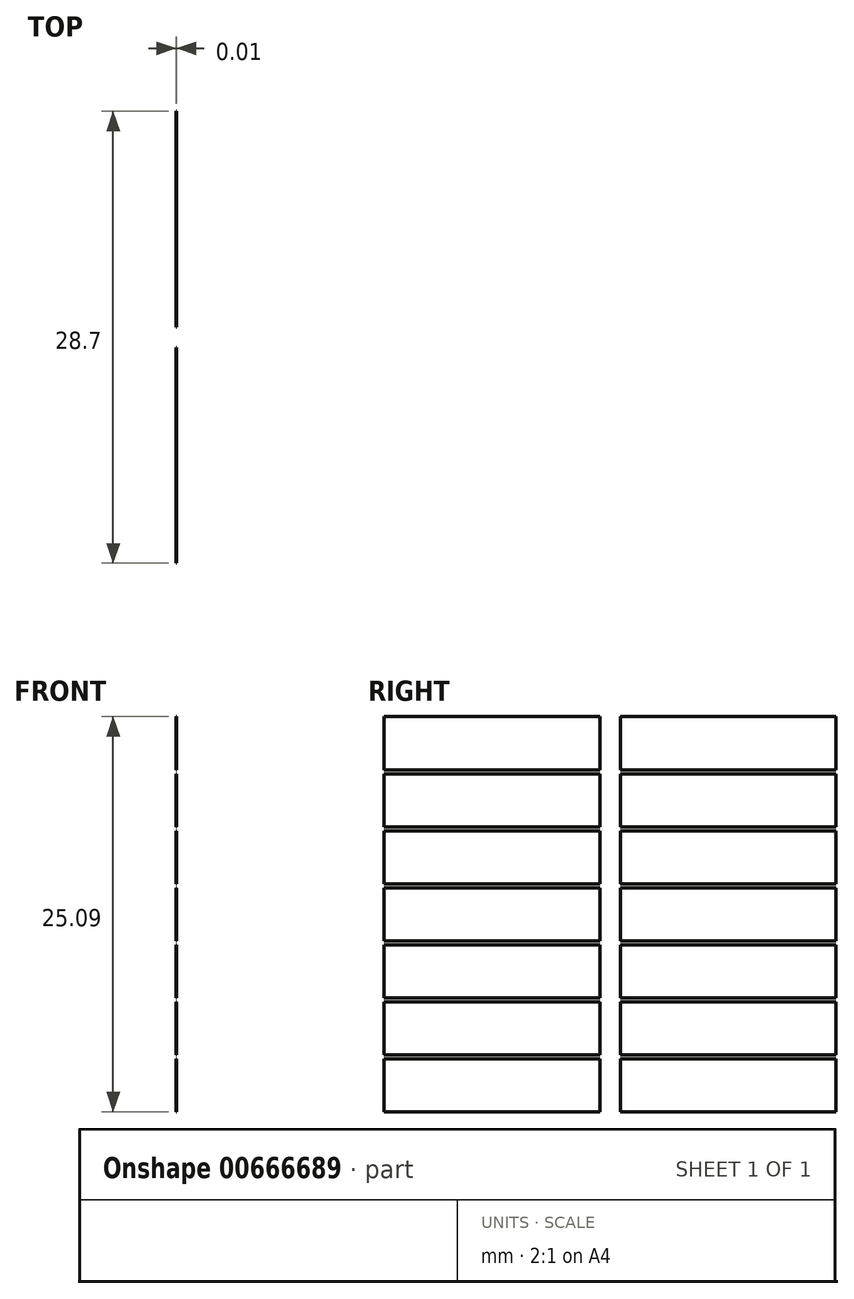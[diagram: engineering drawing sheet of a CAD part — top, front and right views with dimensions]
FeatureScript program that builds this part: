
annotation { "Feature Type Name" : "Feature", "Feature Type Description" : "" }
export const myFeature = defineFeature(function(context is Context, id is Id, definition is map)
    precondition{}
    {
        {
            var Q0;
            Q0=qCreatedBy(makeId("Right.planeOp"),FACE);
            var sketch = newSketch(context, id + "F0", { "sketchPlane" : qUnion([Q0])});
            skPoint(sketch, "E0.0", {"position": v(0, 0) * mm});
            skLineSegment(sketch, "E1.bottom", {"start": v(0, 0) * mm, "end": v(30, 0) * mm});
            skLineSegment(sketch, "E1.top", {"start": v(0, -30) * mm, "end": v(30, -30) * mm});
            skLineSegment(sketch, "E1.left", {"start": v(0, 0) * mm, "end": v(0, -30) * mm});
            skLineSegment(sketch, "E1.right", {"start": v(30, 0) * mm, "end": v(30, -30) * mm});
            skLineSegment(sketch, "E2.1", {"start": v(0.65, -0.65) * mm, "end": v(14.35, -0.65) * mm});
            skLineSegment(sketch, "E2.2", {"start": v(0.65, -0.65) * mm, "end": v(0.65, -2.2) * mm});
            skLineSegment(sketch, "E3", {"start": v(14.35, -2.2) * mm, "end": v(14.35, -0.65) * mm});
            skPoint(sketch, "E4.MirrorP", {"position": v(11.5, 0) * mm});
            skPoint(sketch, "E5.orphan", {"position": v(11.5, -26.74) * mm});
            skPoint(sketch, "E6.orphan", {"position": v(0, -26.74) * mm});
            skLineSegment(sketch, "E7", {"start": v(0.65, -2.46) * mm, "end": v(0.65, -4.02) * mm});
            skLineSegment(sketch, "E8", {"start": v(0.65, -4.02) * mm, "end": v(14.35, -4.02) * mm});
            skLineSegment(sketch, "E9", {"start": v(14.35, -4.02) * mm, "end": v(14.35, -2.46) * mm});
            skLineSegment(sketch, "E10.0", {"start": v(0.65, -4.27) * mm, "end": v(14.35, -4.27) * mm});
            skLineSegment(sketch, "E11", {"start": v(0.65, -4.27) * mm, "end": v(0.65, -5.83) * mm});
            skLineSegment(sketch, "E12", {"start": v(14.35, -5.83) * mm, "end": v(14.35, -4.27) * mm});
            skLineSegment(sketch, "E13.0", {"start": v(0.65, -7.64) * mm, "end": v(14.35, -7.64) * mm});
            skLineSegment(sketch, "E14", {"start": v(0.65, -6.08) * mm, "end": v(0.65, -7.64) * mm});
            skLineSegment(sketch, "E15", {"start": v(14.35, -6.08) * mm, "end": v(14.35, -7.64) * mm});
            skLineSegment(sketch, "E16.0", {"start": v(0.65, -7.9) * mm, "end": v(14.35, -7.9) * mm});
            skLineSegment(sketch, "E17", {"start": v(0.65, -7.9) * mm, "end": v(0.65, -9.45) * mm});
            skLineSegment(sketch, "E18", {"start": v(14.35, -9.45) * mm, "end": v(14.35, -7.9) * mm});
            skLineSegment(sketch, "E19.0", {"start": v(0.65, -11.26) * mm, "end": v(14.35, -11.26) * mm});
            skLineSegment(sketch, "E20", {"start": v(0.65, -9.7) * mm, "end": v(0.65, -11.26) * mm});
            skLineSegment(sketch, "E21", {"start": v(14.35, -9.7) * mm, "end": v(14.35, -11.26) * mm});
            skLineSegment(sketch, "E22.0", {"start": v(0.65, -11.51) * mm, "end": v(14.35, -11.51) * mm});
            skLineSegment(sketch, "E23", {"start": v(0.65, -11.51) * mm, "end": v(0.65, -13.07) * mm});
            skLineSegment(sketch, "E24", {"start": v(14.35, -13.07) * mm, "end": v(14.35, -11.51) * mm});
            skLineSegment(sketch, "E25.0", {"start": v(0.65, -14.88) * mm, "end": v(14.35, -14.88) * mm});
            skLineSegment(sketch, "E26", {"start": v(0.65, -13.32) * mm, "end": v(0.65, -14.88) * mm});
            skLineSegment(sketch, "E27", {"start": v(14.35, -14.88) * mm, "end": v(14.35, -13.32) * mm});
            skLineSegment(sketch, "E28.0", {"start": v(0.65, -15.13) * mm, "end": v(14.35, -15.13) * mm});
            skLineSegment(sketch, "E29", {"start": v(0.65, -15.13) * mm, "end": v(0.65, -16.7) * mm});
            skLineSegment(sketch, "E30", {"start": v(14.35, -16.7) * mm, "end": v(14.35, -15.13) * mm});
            skLineSegment(sketch, "E31.0", {"start": v(0.65, -18.5) * mm, "end": v(14.35, -18.5) * mm});
            skLineSegment(sketch, "E32", {"start": v(0.65, -16.7) * mm, "end": v(0.65, -18.5) * mm});
            skLineSegment(sketch, "E33", {"start": v(14.35, -18.5) * mm, "end": v(14.35, -16.94) * mm});
            skLineSegment(sketch, "E34.0", {"start": v(0.65, -18.75) * mm, "end": v(14.35, -18.75) * mm});
            skLineSegment(sketch, "E35", {"start": v(0.65, -18.75) * mm, "end": v(0.65, -20.31) * mm});
            skLineSegment(sketch, "E36", {"start": v(14.35, -18.75) * mm, "end": v(14.35, -20.31) * mm});
            skLineSegment(sketch, "E37.0", {"start": v(0.65, -22.12) * mm, "end": v(14.35, -22.12) * mm});
            skLineSegment(sketch, "E38", {"start": v(0.65, -20.56) * mm, "end": v(0.65, -22.12) * mm});
            skLineSegment(sketch, "E39", {"start": v(14.35, -20.56) * mm, "end": v(14.35, -22.12) * mm});
            skLineSegment(sketch, "E40.0", {"start": v(0.65, -22.37) * mm, "end": v(14.35, -22.37) * mm});
            skLineSegment(sketch, "E41", {"start": v(0.65, -22.37) * mm, "end": v(0.65, -23.93) * mm});
            skLineSegment(sketch, "E42", {"start": v(14.35, -22.37) * mm, "end": v(14.35, -23.93) * mm});
            skLineSegment(sketch, "E43.0", {"start": v(0.65, -25.74) * mm, "end": v(14.35, -25.74) * mm});
            skLineSegment(sketch, "E44", {"start": v(0.65, -24.18) * mm, "end": v(0.65, -25.74) * mm});
            skLineSegment(sketch, "E45", {"start": v(14.35, -24.18) * mm, "end": v(14.35, -25.74) * mm});
            skLineSegment(sketch, "E46", {"start": v(0.65, -2.46) * mm, "end": v(0.65, -2.2) * mm});
            skLineSegment(sketch, "E47", {"start": v(14.35, -2.46) * mm, "end": v(14.35, -2.2) * mm});
            skLineSegment(sketch, "E48", {"start": v(0.65, -6.08) * mm, "end": v(0.65, -5.83) * mm});
            skLineSegment(sketch, "E49", {"start": v(14.35, -6.08) * mm, "end": v(14.35, -5.83) * mm});
            skLineSegment(sketch, "E50", {"start": v(14.35, -24.18) * mm, "end": v(14.35, -23.93) * mm});
            skLineSegment(sketch, "E51", {"start": v(0.65, -24.18) * mm, "end": v(0.65, -23.93) * mm});
            skLineSegment(sketch, "E52", {"start": v(0.65, -20.56) * mm, "end": v(0.65, -20.31) * mm});
            skLineSegment(sketch, "E53", {"start": v(14.35, -20.56) * mm, "end": v(14.35, -20.31) * mm});
            skLineSegment(sketch, "E54", {"start": v(14.35, -16.94) * mm, "end": v(14.35, -16.7) * mm});
            skLineSegment(sketch, "E55", {"start": v(14.35, -13.32) * mm, "end": v(14.35, -13.07) * mm});
            skLineSegment(sketch, "E56", {"start": v(0.65, -13.32) * mm, "end": v(0.65, -13.07) * mm});
            skLineSegment(sketch, "E57", {"start": v(0.65, -9.7) * mm, "end": v(0.65, -9.45) * mm});
            skLineSegment(sketch, "E58", {"start": v(14.35, -9.7) * mm, "end": v(14.35, -9.45) * mm});
            skLineSegment(sketch, "E59.MirrorCS", {"start": v(29.35, -0.65) * mm, "end": v(29.35, -2.2) * mm});
            skLineSegment(sketch, "E60.MirrorCS", {"start": v(29.35, -2.46) * mm, "end": v(29.35, -2.2) * mm});
            skLineSegment(sketch, "E61.MirrorCS", {"start": v(29.35, -2.46) * mm, "end": v(29.35, -4.02) * mm});
            skLineSegment(sketch, "E62.MirrorCS", {"start": v(29.35, -20.56) * mm, "end": v(29.35, -22.12) * mm});
            skLineSegment(sketch, "E63.MirrorCS", {"start": v(15.65, -4.02) * mm, "end": v(15.65, -2.46) * mm});
            skLineSegment(sketch, "E64.MirrorCS", {"start": v(29.35, -20.56) * mm, "end": v(29.35, -20.31) * mm});
            skLineSegment(sketch, "E65.MirrorCS", {"start": v(29.35, -7.9) * mm, "end": v(29.35, -9.45) * mm});
            skLineSegment(sketch, "E66.MirrorCS", {"start": v(15.65, -16.7) * mm, "end": v(15.65, -15.13) * mm});
            skLineSegment(sketch, "E67.MirrorCS", {"start": v(29.35, -9.7) * mm, "end": v(29.35, -9.45) * mm});
            skLineSegment(sketch, "E68.MirrorCS", {"start": v(29.35, -6.08) * mm, "end": v(29.35, -5.83) * mm});
            skLineSegment(sketch, "E69.MirrorCS", {"start": v(15.65, -9.7) * mm, "end": v(15.65, -9.45) * mm});
            skLineSegment(sketch, "E70.MirrorCS", {"start": v(15.65, -22.37) * mm, "end": v(15.65, -23.93) * mm});
            skLineSegment(sketch, "E71.MirrorCS", {"start": v(29.35, -24.18) * mm, "end": v(29.35, -23.93) * mm});
            skLineSegment(sketch, "E72.MirrorCS", {"start": v(29.35, -4.27) * mm, "end": v(29.35, -5.83) * mm});
            skLineSegment(sketch, "E73.MirrorCS", {"start": v(15.65, -20.56) * mm, "end": v(15.65, -20.31) * mm});
            skLineSegment(sketch, "E74.MirrorCS", {"start": v(15.65, -9.45) * mm, "end": v(15.65, -7.9) * mm});
            skLineSegment(sketch, "E75.MirrorCS", {"start": v(29.35, -11.51) * mm, "end": v(29.35, -13.07) * mm});
            skLineSegment(sketch, "E76.MirrorCS", {"start": v(29.35, -13.32) * mm, "end": v(29.35, -13.07) * mm});
            skLineSegment(sketch, "E77.MirrorCS", {"start": v(15.65, -6.08) * mm, "end": v(15.65, -7.64) * mm});
            skLineSegment(sketch, "E78.MirrorCS", {"start": v(15.65, -14.88) * mm, "end": v(15.65, -13.32) * mm});
            skLineSegment(sketch, "E79.MirrorCS", {"start": v(29.35, -18.75) * mm, "end": v(29.35, -20.31) * mm});
            skLineSegment(sketch, "E80.MirrorCS", {"start": v(15.65, -24.18) * mm, "end": v(15.65, -23.93) * mm});
            skLineSegment(sketch, "E81.MirrorCS", {"start": v(29.35, -6.08) * mm, "end": v(29.35, -7.64) * mm});
            skLineSegment(sketch, "E82.MirrorCS", {"start": v(29.35, -13.32) * mm, "end": v(29.35, -14.88) * mm});
            skLineSegment(sketch, "E83.MirrorCS", {"start": v(15.65, -6.08) * mm, "end": v(15.65, -5.83) * mm});
            skLineSegment(sketch, "E84.MirrorCS", {"start": v(15.65, -18.5) * mm, "end": v(15.65, -16.94) * mm});
            skLineSegment(sketch, "E85.MirrorCS", {"start": v(29.35, -9.7) * mm, "end": v(29.35, -11.26) * mm});
            skLineSegment(sketch, "E86.MirrorCS", {"start": v(15.65, -13.07) * mm, "end": v(15.65, -11.51) * mm});
            skLineSegment(sketch, "E87.MirrorCS", {"start": v(15.65, -20.56) * mm, "end": v(15.65, -22.12) * mm});
            skLineSegment(sketch, "E88.MirrorCS", {"start": v(15.65, -13.32) * mm, "end": v(15.65, -13.07) * mm});
            skLineSegment(sketch, "E89.MirrorCS", {"start": v(15.65, -5.83) * mm, "end": v(15.65, -4.27) * mm});
            skLineSegment(sketch, "E90.MirrorCS", {"start": v(15.65, -9.7) * mm, "end": v(15.65, -11.26) * mm});
            skLineSegment(sketch, "E91.MirrorCS", {"start": v(29.35, -22.37) * mm, "end": v(29.35, -23.93) * mm});
            skLineSegment(sketch, "E92.MirrorCS", {"start": v(15.65, -18.75) * mm, "end": v(15.65, -20.31) * mm});
            skLineSegment(sketch, "E93.MirrorCS", {"start": v(29.35, -16.7) * mm, "end": v(29.35, -18.5) * mm});
            skLineSegment(sketch, "E94.MirrorCS", {"start": v(15.65, -2.2) * mm, "end": v(15.65, -0.65) * mm});
            skLineSegment(sketch, "E95.MirrorCS", {"start": v(29.35, -24.18) * mm, "end": v(29.35, -25.74) * mm});
            skLineSegment(sketch, "E96.MirrorCS", {"start": v(29.35, -15.13) * mm, "end": v(29.35, -16.7) * mm});
            skLineSegment(sketch, "E97.MirrorCS", {"start": v(15.65, -24.18) * mm, "end": v(15.65, -25.74) * mm});
            skLineSegment(sketch, "E98.MirrorCS", {"start": v(29.35, -4.02) * mm, "end": v(15.65, -4.02) * mm});
            skPoint(sketch, "E99.MirrorP", {"position": v(18.5, 0) * mm});
            skPoint(sketch, "E100.MirrorP", {"position": v(30, 0) * mm});
            skLineSegment(sketch, "E101.MirrorCS", {"start": v(29.35, -14.88) * mm, "end": v(15.65, -14.88) * mm});
            skLineSegment(sketch, "E102.MirrorCS", {"start": v(29.35, -0.65) * mm, "end": v(15.65, -0.65) * mm});
            skPoint(sketch, "E103.MirrorP", {"position": v(30, -26.74) * mm});
            skLineSegment(sketch, "E104.MirrorCS", {"start": v(29.35, -11.26) * mm, "end": v(15.65, -11.26) * mm});
            skLineSegment(sketch, "E105.MirrorCS", {"start": v(29.35, -18.75) * mm, "end": v(15.65, -18.75) * mm});
            skLineSegment(sketch, "E106.MirrorCS", {"start": v(29.35, -11.51) * mm, "end": v(15.65, -11.51) * mm});
            skLineSegment(sketch, "E107.MirrorCS", {"start": v(29.35, -22.37) * mm, "end": v(15.65, -22.37) * mm});
            skLineSegment(sketch, "E108.MirrorCS", {"start": v(29.35, -7.9) * mm, "end": v(15.65, -7.9) * mm});
            skLineSegment(sketch, "E109.MirrorCS", {"start": v(29.35, -25.74) * mm, "end": v(15.65, -25.74) * mm});
            skLineSegment(sketch, "E110.MirrorCS", {"start": v(29.35, -15.13) * mm, "end": v(15.65, -15.13) * mm});
            skLineSegment(sketch, "E111.MirrorCS", {"start": v(29.35, -4.27) * mm, "end": v(15.65, -4.27) * mm});
            skLineSegment(sketch, "E112.MirrorCS", {"start": v(29.35, -18.5) * mm, "end": v(15.65, -18.5) * mm});
            skLineSegment(sketch, "E113.MirrorCS", {"start": v(29.35, -7.64) * mm, "end": v(15.65, -7.64) * mm});
            skLineSegment(sketch, "E114.MirrorCS", {"start": v(29.35, -22.12) * mm, "end": v(15.65, -22.12) * mm});
            skPoint(sketch, "E115.MirrorP", {"position": v(18.5, -26.74) * mm});
            skLineSegment(sketch, "E116", {"start": v(15.65, -2.46) * mm, "end": v(15.65, -2.2) * mm});
            skLineSegment(sketch, "E117", {"start": v(15.65, -16.94) * mm, "end": v(15.65, -16.7) * mm});
            skSolve(sketch);
        }
        {
            var Q0;
            Q0=makeQuery(id+"F0.imprint","IMPRINT",FACE,{"disambiguationData":[TD([[makeQuery(id+"F0.imprint","IMPRINT",EDGE,{"derivedFrom":sQuery(id+"F0.wireOp",EDGE,"14657d91-79c0-4d6f-9dc8-bfef05761bba.0")}),1.0]])]});
            var Q1;
            Q1=makeQuery(id+"F0.imprint","IMPRINT",FACE,{"disambiguationData":[TD([[makeQuery(id+"F0.imprint","IMPRINT",EDGE,{"derivedFrom":sQuery(id+"F0.wireOp",EDGE,"d10a1318-4c6c-4e2f-b301-627ccdfaac9c.0")}),1.0]])]});
            var Q2;
            Q2=makeQuery(id+"F0.imprint","IMPRINT",FACE,{"disambiguationData":[TD([[makeQuery(id+"F0.imprint","IMPRINT",EDGE,{"derivedFrom":sQuery(id+"F0.wireOp",EDGE,"34b941e1-9213-4a0b-9b3c-3fd5b53a19226.MirrorCS")}),1.0]])]});
            var Q3;
            Q3=makeQuery(id+"F0.imprint","IMPRINT",FACE,{"disambiguationData":[TD([[makeQuery(id+"F0.imprint","IMPRINT",EDGE,{"derivedFrom":sQuery(id+"F0.wireOp",EDGE,"e52c6cc0-2e10-4916-a505-43da0128bf07.0")}),-1.0]])]});
            var Q4;
            Q4=makeQuery(id+"F0.imprint","IMPRINT",FACE,{"disambiguationData":[TD([[makeQuery(id+"F0.imprint","IMPRINT",EDGE,{"derivedFrom":sQuery(id+"F0.wireOp",EDGE,"34b941e1-9213-4a0b-9b3c-3fd5b53a19229.MirrorCS")}),1.0]])]});
            var Q5;
            Q5=makeQuery(id+"F0.imprint","IMPRINT",FACE,{"disambiguationData":[TD([[makeQuery(id+"F0.imprint","IMPRINT",EDGE,{"derivedFrom":sQuery(id+"F0.wireOp",EDGE,"34b941e1-9213-4a0b-9b3c-3fd5b53a19223.MirrorCS")}),1.0]])]});
            var Q6;
            Q6=makeQuery(id+"F0.imprint","IMPRINT",FACE,{"disambiguationData":[TD([[makeQuery(id+"F0.imprint","IMPRINT",EDGE,{"derivedFrom":sQuery(id+"F0.wireOp",EDGE,"E2.1")}),-1.0]])]});
            var Q7;
            Q7=makeQuery(id+"F0.imprint","IMPRINT",FACE,{"disambiguationData":[TD([[makeQuery(id+"F0.imprint","IMPRINT",EDGE,{"derivedFrom":sQuery(id+"F0.wireOp",EDGE,"34b941e1-9213-4a0b-9b3c-3fd5b53a19222.MirrorCS")}),1.0]])]});
            var Q8;
            Q8=makeQuery(id+"F0.imprint","IMPRINT",FACE,{"disambiguationData":[TD([[makeQuery(id+"F0.imprint","IMPRINT",EDGE,{"derivedFrom":sQuery(id+"F0.wireOp",EDGE,"34b941e1-9213-4a0b-9b3c-3fd5b53a19224.MirrorCS")}),1.0]])]});
            var Q9;
            Q9=makeQuery(id+"F0.imprint","IMPRINT",FACE,{"disambiguationData":[TD([[makeQuery(id+"F0.imprint","IMPRINT",EDGE,{"derivedFrom":sQuery(id+"F0.wireOp",EDGE,"34b941e1-9213-4a0b-9b3c-3fd5b53a19221.MirrorCS")}),-1.0]])]});
            var Q10;
            Q10=makeQuery(id+"F0.imprint","IMPRINT",FACE,{"disambiguationData":[TD([[makeQuery(id+"F0.imprint","IMPRINT",EDGE,{"derivedFrom":sQuery(id+"F0.wireOp",EDGE,"7f593fd2-97bd-4d00-b395-f38d8aa9202c.0")}),1.0]])]});
            var Q11;
            Q11=makeQuery(id+"F0.imprint","IMPRINT",FACE,{"disambiguationData":[TD([[makeQuery(id+"F0.imprint","IMPRINT",EDGE,{"derivedFrom":sQuery(id+"F0.wireOp",EDGE,"7881708b-2482-4012-b24c-5590632c987f.0")}),1.0]])]});
            var Q12;
            Q12=makeQuery(id+"F0.imprint","IMPRINT",FACE,{"disambiguationData":[TD([[makeQuery(id+"F0.imprint","IMPRINT",EDGE,{"derivedFrom":sQuery(id+"F0.wireOp",EDGE,"b2c296a6-979c-4eb4-8951-c574cebceffd.0")}),1.0]])]});
            var Q13;
            Q13=makeQuery(id+"F0.imprint","IMPRINT",FACE,{"disambiguationData":[TD([[makeQuery(id+"F0.imprint","IMPRINT",EDGE,{"derivedFrom":sQuery(id+"F0.wireOp",EDGE,"E2.0")}),-1.0]])]});
            var Q14;
            Q14=makeQuery(id+"F0.imprint","IMPRINT",FACE,{"disambiguationData":[TD([[makeQuery(id+"F0.imprint","IMPRINT",EDGE,{"derivedFrom":sQuery(id+"F0.wireOp",EDGE,"E10.0")}),-1.0]])]});
            var Q15;
            Q15=makeQuery(id+"F0.imprint","IMPRINT",FACE,{"disambiguationData":[TD([[makeQuery(id+"F0.imprint","IMPRINT",EDGE,{"derivedFrom":sQuery(id+"F0.wireOp",EDGE,"E22.0")}),-1.0]])]});
            var Q16;
            Q16=makeQuery(id+"F0.imprint","IMPRINT",FACE,{"disambiguationData":[TD([[makeQuery(id+"F0.imprint","IMPRINT",EDGE,{"derivedFrom":sQuery(id+"F0.wireOp",EDGE,"E16.0")}),-1.0]])]});
            var Q17;
            Q17=makeQuery(id+"F0.imprint","IMPRINT",FACE,{"disambiguationData":[TD([[makeQuery(id+"F0.imprint","IMPRINT",EDGE,{"derivedFrom":sQuery(id+"F0.wireOp",EDGE,"E28.0")}),-1.0]])]});
            var Q18;
            Q18=makeQuery(id+"F0.imprint","IMPRINT",FACE,{"disambiguationData":[TD([[makeQuery(id+"F0.imprint","IMPRINT",EDGE,{"derivedFrom":sQuery(id+"F0.wireOp",EDGE,"E34.0")}),-1.0]])]});
            var Q19;
            Q19=makeQuery(id+"F0.imprint","IMPRINT",FACE,{"disambiguationData":[TD([[makeQuery(id+"F0.imprint","IMPRINT",EDGE,{"derivedFrom":sQuery(id+"F0.wireOp",EDGE,"E40.0")}),-1.0]])]});
            var Q20;
            Q20=makeQuery(id+"F0.imprint","IMPRINT",FACE,{"disambiguationData":[TD([[makeQuery(id+"F0.imprint","IMPRINT",EDGE,{"derivedFrom":sQuery(id+"F0.wireOp",EDGE,"E70.MirrorCS")}),1.0]])]});
            var Q21;
            Q21=makeQuery(id+"F0.imprint","IMPRINT",FACE,{"disambiguationData":[TD([[makeQuery(id+"F0.imprint","IMPRINT",EDGE,{"derivedFrom":sQuery(id+"F0.wireOp",EDGE,"E68.MirrorCS")}),1.0]])]});
            var Q22;
            Q22=makeQuery(id+"F0.imprint","IMPRINT",FACE,{"disambiguationData":[TD([[makeQuery(id+"F0.imprint","IMPRINT",EDGE,{"derivedFrom":sQuery(id+"F0.wireOp",EDGE,"E65.MirrorCS")}),-1.0]])]});
            var Q23;
            Q23=makeQuery(id+"F0.imprint","IMPRINT",FACE,{"disambiguationData":[TD([[makeQuery(id+"F0.imprint","IMPRINT",EDGE,{"derivedFrom":sQuery(id+"F0.wireOp",EDGE,"E75.MirrorCS")}),-1.0]])]});
            var Q24;
            Q24=makeQuery(id+"F0.imprint","IMPRINT",FACE,{"disambiguationData":[TD([[makeQuery(id+"F0.imprint","IMPRINT",EDGE,{"derivedFrom":sQuery(id+"F0.wireOp",EDGE,"E62.MirrorCS")}),-1.0]])]});
            var Q25;
            Q25=makeQuery(id+"F0.imprint","IMPRINT",FACE,{"disambiguationData":[TD([[makeQuery(id+"F0.imprint","IMPRINT",EDGE,{"derivedFrom":sQuery(id+"F0.wireOp",EDGE,"E66.MirrorCS")}),-1.0]])]});
            var Q26;
            Q26=makeQuery(id+"F0.imprint","IMPRINT",FACE,{"disambiguationData":[TD([[makeQuery(id+"F0.imprint","IMPRINT",EDGE,{"derivedFrom":sQuery(id+"F0.wireOp",EDGE,"E60.MirrorCS")}),1.0]])]});
            extrude(context, id + "F1", {"entities" : qUnion([Q0, Q1, Q2, Q3, Q4, Q5, Q6, Q7, Q8, Q9, Q10, Q11, Q12, Q13, Q14, Q15, Q16, Q17, Q18, Q19, Q20, Q21, Q22, Q23, Q24, Q25, Q26]), "depth" : 0.01 * mm, "offsetDistance" : 25 * mm});
        }
    });
